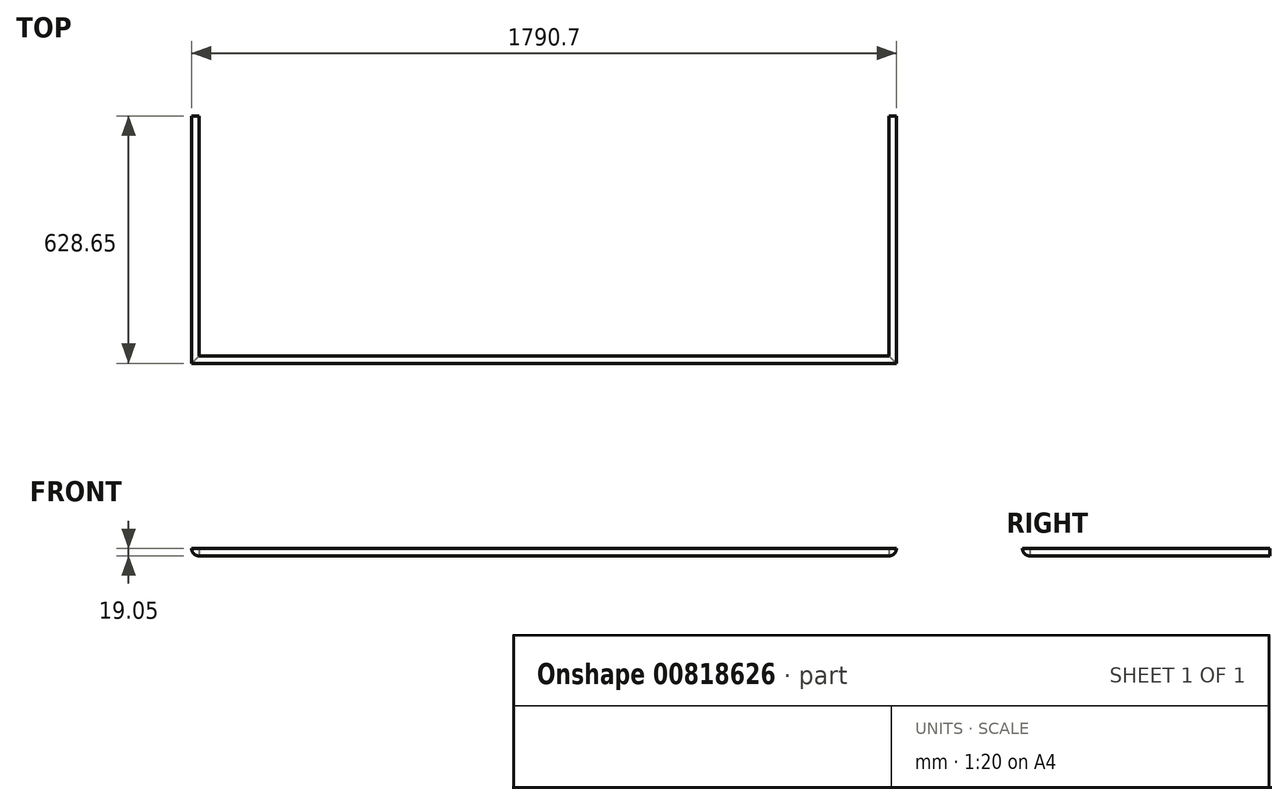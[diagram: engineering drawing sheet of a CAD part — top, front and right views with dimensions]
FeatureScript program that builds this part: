
annotation { "Feature Type Name" : "Feature", "Feature Type Description" : "" }
export const myFeature = defineFeature(function(context is Context, id is Id, definition is map)
    precondition{}
    {
        {
            var Q0;
            Q0=qCreatedBy(makeId("Top.planeOp"),FACE);
            var sketch = newSketch(context, id + "F0", { "sketchPlane" : qUnion([Q0])});
            skLineSegment(sketch, "E0.bottom", {"start": v(876.3, -304.8) * mm, "end": v(-876.3, -304.8) * mm});
            skLineSegment(sketch, "E0.left", {"start": v(876.3, -304.8) * mm, "end": v(876.3, 304.8) * mm});
            skLineSegment(sketch, "E0.right", {"start": v(-876.3, -304.8) * mm, "end": v(-876.3, 304.8) * mm});
            skPoint(sketch, "E0.middle", {"position": v(0, 0) * mm});
            skLineSegment(sketch, "E1.left", {"start": v(895.35, -323.85) * mm, "end": v(895.35, 304.8) * mm});
            skLineSegment(sketch, "E1.right", {"start": v(-895.35, -323.85) * mm, "end": v(-895.35, 304.8) * mm});
            skLineSegment(sketch, "E2", {"start": v(876.3, 304.8) * mm, "end": v(895.35, 304.8) * mm});
            skLineSegment(sketch, "E3", {"start": v(-876.3, 304.8) * mm, "end": v(-895.35, 304.8) * mm});
            skPoint(sketch, "E4.orphan", {"position": v(-895.35, 413.12) * mm});
            skPoint(sketch, "E5.orphan", {"position": v(895.35, 413.12) * mm});
            skLineSegment(sketch, "E6", {"start": v(895.35, -323.85) * mm, "end": v(-895.35, -323.85) * mm});
            skPoint(sketch, "E1.bottom.start.orphan", {"position": v(895.35, -413.12) * mm});
            skPoint(sketch, "E7.orphan", {"position": v(-895.35, -413.12) * mm});
            skSolve(sketch);
        }
        {
            var Q0;
            Q0 = qSketchRegion(id + "F0", true);
            extrude(context, id + "F1", {"entities" : qUnion([Q0]), "depth" : 19.05 * mm, "offsetDistance" : 25.4 * mm});
        }
        {
            var Q0;
            Q0=makeQuery(id+"F1.opExtrude","CAP_EDGE",EDGE,{"disambiguationData":[OSD([sQuery(id+"F0.wireOp",EDGE,"E1.right")])],"isStart":true});
            var Q1;
            Q1=makeQuery(id+"F1.opExtrude","CAP_EDGE",EDGE,{"disambiguationData":[OSD([sQuery(id+"F0.wireOp",EDGE,"E6")])],"isStart":true});
            var Q2;
            Q2=makeQuery(id+"F1.opExtrude","CAP_EDGE",EDGE,{"disambiguationData":[OSD([sQuery(id+"F0.wireOp",EDGE,"E1.left")])],"isStart":true});
            fillet(context, id + "F2", {"entities" : qUnion([Q0, Q1, Q2]), "radius" : 19.05 * mm, "tangentPropagation" : true, "allowEdgeOverflow" : false});
        }
    });
